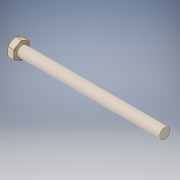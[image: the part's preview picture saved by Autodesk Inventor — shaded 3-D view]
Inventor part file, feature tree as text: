
AUTODESK INVENTOR PART (.ipt)
format: ipt  version: 2016 (Build 200138000, 138)  size: 134,144 bytes
history: native  units: in
note: dims shown in document units (in); Inventor stores cm internally (conversion verified against a paired STEP export)
features: extrude x2, sketch x2, projected_geometry x1, other x1
ambient origin geometry x8: Origin, YZ Plane, XZ Plane, XY Plane, X Axis, Y Axis, Z Axis, Center Point
bodies: Solid1 (feature_tree)
feature tree (6):
  extrude  "Extrusion1"  Depth=1.047in TaperAngle=0.0deg
  extrude  "Extrusion2"  [1 undecoded]
  sketch  "Sketch1"  dims[d0=0.04in d1=0.0in d2=1.047in d3=0.0in]
  sketch  "Sketch2"
  projected_geometry  "Projected Loop1"
  other  "HeadFillet"
note: 1 required parameter value undecoded (feature->parameter linkage not recoverable at this tier; creation-order binding heuristic only, values carry confidence <= 0.55)
